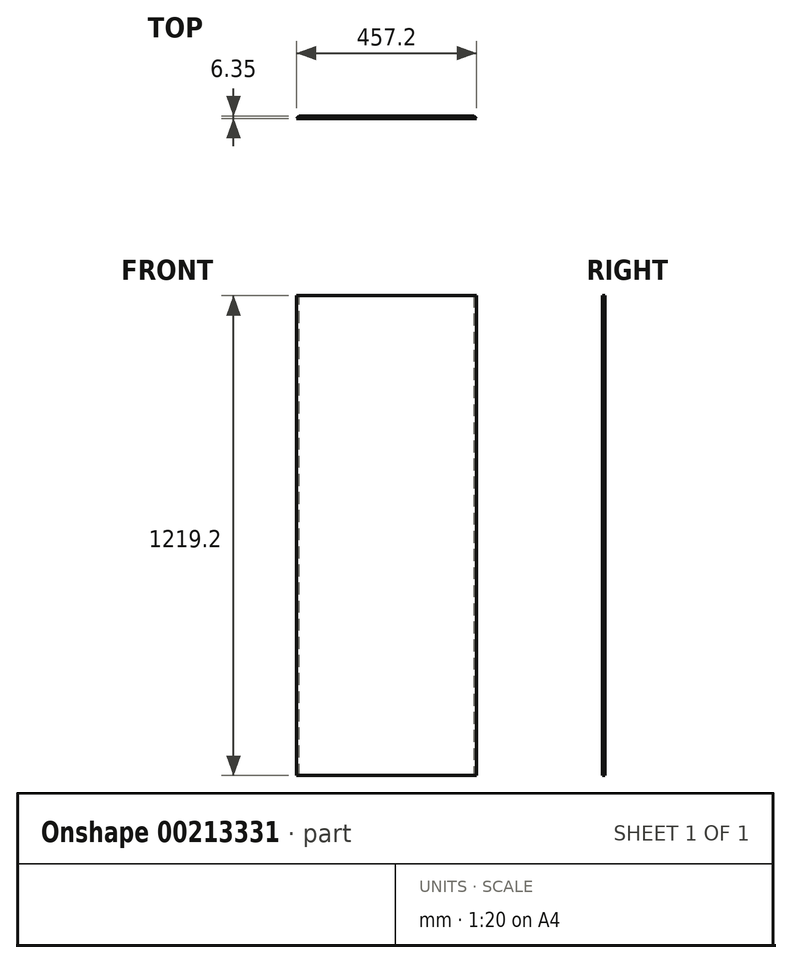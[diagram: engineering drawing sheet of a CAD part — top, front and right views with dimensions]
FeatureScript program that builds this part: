
annotation { "Feature Type Name" : "Feature", "Feature Type Description" : "" }
export const myFeature = defineFeature(function(context is Context, id is Id, definition is map)
    precondition{}
    {
        {
            var Q0;
            Q0=qCreatedBy(makeId("Front.planeOp"),FACE);
            var sketch = newSketch(context, id + "F0", { "sketchPlane" : qUnion([Q0])});
            skLineSegment(sketch, "E0.bottom", {"start": v(228.6, 609.6) * mm, "end": v(-228.6, 609.6) * mm});
            skLineSegment(sketch, "E0.top", {"start": v(228.6, -609.6) * mm, "end": v(-228.6, -609.6) * mm});
            skLineSegment(sketch, "E0.left", {"start": v(228.6, 609.6) * mm, "end": v(228.6, -609.6) * mm});
            skLineSegment(sketch, "E0.right", {"start": v(-228.6, 609.6) * mm, "end": v(-228.6, -609.6) * mm});
            skPoint(sketch, "E0.middle", {"position": v(0, 0) * mm});
            skSolve(sketch);
        }
        {
            var Q0;
            Q0 = qSketchRegion(id + "F0", true);
            extrude(context, id + "F1", {"entities" : qUnion([Q0]), "depth" : 6.35 * mm});
        }
        {
            var Q0;
            Q0=makeQuery(id+"F1.opExtrude","CAP_EDGE",EDGE,{"disambiguationData":[OSD([sQuery(id+"F0.wireOp",EDGE,"E0.right")])],"isStart":true});
            chamfer(context, id + "F2", {"entities" : qUnion([Q0]), "width" : 6.35 * mm, "tangentPropagation" : true});
        }
        {
            var Q0;
            Q0=makeQuery(id+"F1.opExtrude","CAP_EDGE",EDGE,{"disambiguationData":[OSD([sQuery(id+"F0.wireOp",EDGE,"E0.left")])],"isStart":true});
            chamfer(context, id + "F3", {"entities" : qUnion([Q0]), "width" : 6.35 * mm, "tangentPropagation" : true});
        }
    });
